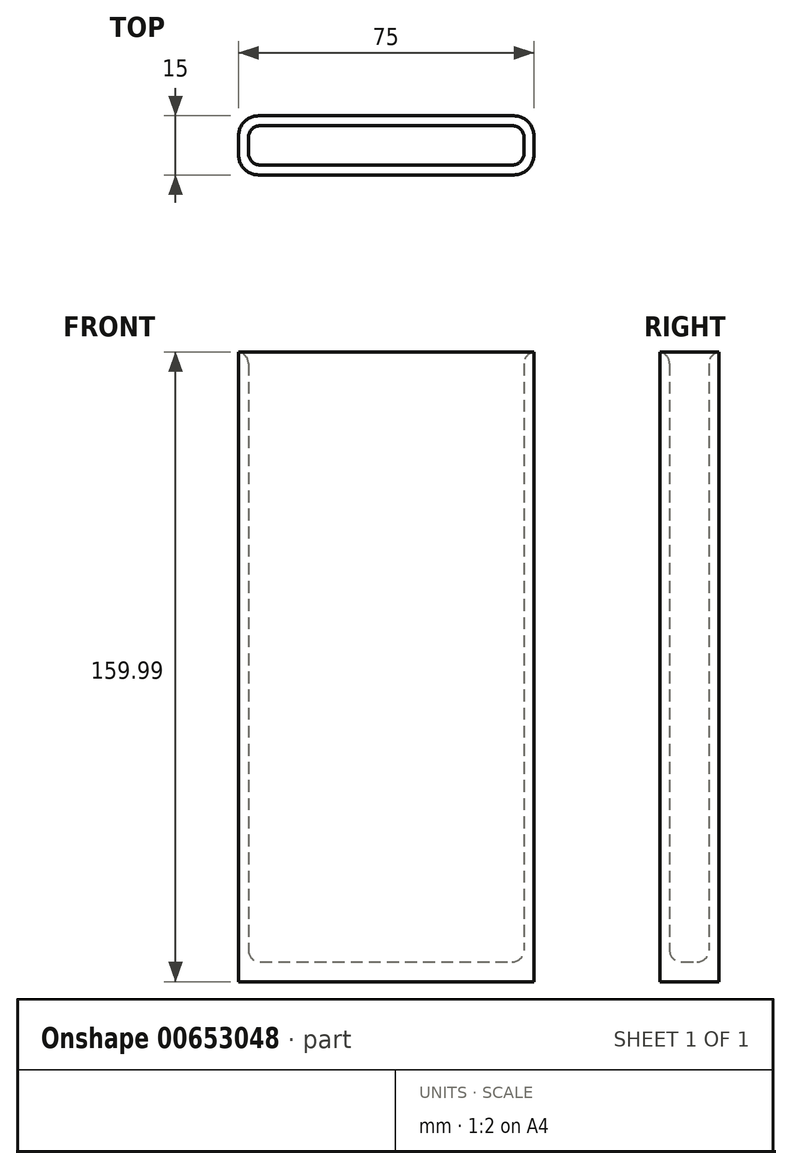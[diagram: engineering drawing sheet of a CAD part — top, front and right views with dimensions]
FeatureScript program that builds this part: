
annotation { "Feature Type Name" : "Feature", "Feature Type Description" : "" }
export const myFeature = defineFeature(function(context is Context, id is Id, definition is map)
    precondition{}
    {
        {
            var Q0;
            Q0=qCreatedBy(makeId("Top.planeOp"),FACE);
            var sketch = newSketch(context, id + "F0", { "sketchPlane" : qUnion([Q0])});
            skLineSegment(sketch, "E0.0", {"start": v(-72.5, -2.5) * mm, "end": v(2.5, -2.5) * mm});
            skLineSegment(sketch, "E0.1", {"start": v(-72.5, -2.5) * mm, "end": v(-72.5, 12.5) * mm});
            skLineSegment(sketch, "E0.2", {"start": v(2.5, 12.5) * mm, "end": v(-72.5, 12.5) * mm});
            skLineSegment(sketch, "E0.3", {"start": v(2.5, -2.5) * mm, "end": v(2.5, 12.5) * mm});
            skSolve(sketch);
        }
        {
            var Q0;
            Q0=makeQuery(id+"F0.imprint","IMPRINT",FACE,{"disambiguationData":[TD([[makeQuery(id+"F0.imprint","IMPRINT",EDGE,{"derivedFrom":sQuery(id+"F0.wireOp",EDGE,"E0.0")}),1.0]])]});
            extrude(context, id + "F1", {"entities" : qUnion([Q0]), "depth" : 5 * mm, "offsetDistance" : 25 * mm});
        }
        {
            var Q0;
            Q0=makeQuery(id+"F1.opExtrude","CAP_FACE",FACE,{"disambiguationData":[OSD([sQuery(id+"F0.wireOp",EDGE,"E0.0"),sQuery(id+"F0.wireOp",EDGE,"E0.1"),sQuery(id+"F0.wireOp",EDGE,"E0.2"),sQuery(id+"F0.wireOp",EDGE,"E0.3")])],"isStart":true});
            var sketch = newSketch(context, id + "F2", { "sketchPlane" : qUnion([Q0])});
            skLineSegment(sketch, "E1.0", {"start": v(0, 0) * mm, "end": v(-70, 0) * mm});
            skLineSegment(sketch, "E1.1", {"start": v(0, -10) * mm, "end": v(0, 0) * mm});
            skLineSegment(sketch, "E1.2", {"start": v(-70, -10) * mm, "end": v(0, -10) * mm});
            skLineSegment(sketch, "E1.3", {"start": v(-70, 0) * mm, "end": v(-70, -10) * mm});
            skSolve(sketch);
        }
        {
            var Q0;
            Q0=makeQuery(id+"F2.imprint","IMPRINT",FACE,{"disambiguationData":[TD([[makeQuery(id+"F2.imprint","IMPRINT",EDGE,{"derivedFrom":sQuery(id+"F2.wireOp",EDGE,"E1.0")}),-1.0]])]});
            extrude(context, id + "F3", {"entities" : qUnion([Q0]), "operationType" : NewBodyOperationType.ADD, "oppositeDirection" : true, "depth" : 160 * mm, "offsetDistance" : 25 * mm});
        }
        {
            var Q0;
            {var subQ0=sQuery(id+"F0.wireOp",EDGE,"E0.2");var subQ1=sQuery(id+"F0.wireOp",EDGE,"E0.1");Q0=makeQuery(id+"F3.boolean.opBoolean","MERGE",EDGE,{"derivedFrom":[makeQuery(id+"F1.opExtrude","SWEPT_EDGE",EDGE,{"disambiguationData":[OSD([subQ1,subQ0])]}),makeQuery(id+"F3.opExtrude","SWEPT_EDGE",EDGE,{"disambiguationData":[OSD([subQ1,subQ0])]})]});}
            fillet(context, id + "F4", {"entities" : qUnion([Q0]), "radius" : 5 * mm, "tangentPropagation" : true, "allowEdgeOverflow" : false});
        }
        {
            var Q0;
            {var subQ0=sQuery(id+"F0.wireOp",EDGE,"E0.1");var subQ1=sQuery(id+"F0.wireOp",EDGE,"E0.0");Q0=makeQuery(id+"F3.boolean.opBoolean","MERGE",EDGE,{"derivedFrom":[makeQuery(id+"F1.opExtrude","SWEPT_EDGE",EDGE,{"disambiguationData":[OSD([subQ1,subQ0])]}),makeQuery(id+"F3.opExtrude","SWEPT_EDGE",EDGE,{"disambiguationData":[OSD([subQ1,subQ0])]})]});}
            fillet(context, id + "F5", {"entities" : qUnion([Q0]), "radius" : 5 * mm, "tangentPropagation" : true, "allowEdgeOverflow" : false});
        }
        {
            var Q0;
            {var subQ0=sQuery(id+"F0.wireOp",EDGE,"E0.3");var subQ1=sQuery(id+"F0.wireOp",EDGE,"E0.0");Q0=makeQuery(id+"F3.boolean.opBoolean","MERGE",EDGE,{"derivedFrom":[makeQuery(id+"F1.opExtrude","SWEPT_EDGE",EDGE,{"disambiguationData":[OSD([subQ1,subQ0])]}),makeQuery(id+"F3.opExtrude","SWEPT_EDGE",EDGE,{"disambiguationData":[OSD([subQ1,subQ0])]})]});}
            fillet(context, id + "F6", {"entities" : qUnion([Q0]), "radius" : 5 * mm, "tangentPropagation" : true, "allowEdgeOverflow" : false});
        }
        {
            var Q0;
            {var subQ0=sQuery(id+"F0.wireOp",EDGE,"E0.3");var subQ1=sQuery(id+"F0.wireOp",EDGE,"E0.2");Q0=makeQuery(id+"F3.boolean.opBoolean","MERGE",EDGE,{"derivedFrom":[makeQuery(id+"F1.opExtrude","SWEPT_EDGE",EDGE,{"disambiguationData":[OSD([subQ1,subQ0])]}),makeQuery(id+"F3.opExtrude","SWEPT_EDGE",EDGE,{"disambiguationData":[OSD([subQ1,subQ0])]})]});}
            fillet(context, id + "F7", {"entities" : qUnion([Q0]), "radius" : 5 * mm, "tangentPropagation" : true, "allowEdgeOverflow" : false});
        }
        {
            var Q0;
            Q0=makeQuery(id+"F3.opExtrude","SWEPT_EDGE",EDGE,{"disambiguationData":[OSD([sQuery(id+"F2.wireOp",EDGE,"E1.2"),sQuery(id+"F2.wireOp",EDGE,"E1.3")])]});
            fillet(context, id + "F8", {"entities" : qUnion([Q0]), "radius" : 3 * mm, "tangentPropagation" : true, "allowEdgeOverflow" : false});
        }
        {
            var Q0;
            Q0=makeQuery(id+"F3.opExtrude","SWEPT_EDGE",EDGE,{"disambiguationData":[OSD([sQuery(id+"F2.wireOp",EDGE,"E1.1"),sQuery(id+"F2.wireOp",EDGE,"E1.2")])]});
            fillet(context, id + "F9", {"entities" : qUnion([Q0]), "radius" : 3 * mm, "tangentPropagation" : true, "allowEdgeOverflow" : false});
        }
        {
            var Q0;
            Q0=makeQuery(id+"F3.opExtrude","SWEPT_EDGE",EDGE,{"disambiguationData":[OSD([sQuery(id+"F2.wireOp",EDGE,"E1.0"),sQuery(id+"F2.wireOp",EDGE,"E1.3")])]});
            fillet(context, id + "F10", {"entities" : qUnion([Q0]), "radius" : 3 * mm, "tangentPropagation" : true, "allowEdgeOverflow" : false});
        }
        {
            var Q0;
            Q0=makeQuery(id+"F3.opExtrude","SWEPT_EDGE",EDGE,{"disambiguationData":[OSD([sQuery(id+"F2.wireOp",EDGE,"E1.0"),sQuery(id+"F2.wireOp",EDGE,"E1.1")])]});
            fillet(context, id + "F11", {"entities" : qUnion([Q0]), "radius" : 3 * mm, "tangentPropagation" : true, "allowEdgeOverflow" : false});
        }
        {
            var Q0;
            Q0=makeQuery(id+"F3.opExtrude","CAP_EDGE",EDGE,{"disambiguationData":[OSD([sQuery(id+"F2.wireOp",EDGE,"E1.3")])],"isStart":false});
            var Q1;
            {var subQ0=sQuery(id+"F2.wireOp",EDGE,"E1.3");var subQ1=sQuery(id+"F2.wireOp",EDGE,"E1.2");Q1=makeQuery(id+"F8.opFillet","BLEND_EDGE",EDGE,{"blendedFrom":[makeQuery(id+"F3.opExtrude","SWEPT_EDGE",EDGE,{"disambiguationData":[OSD([subQ1,subQ0])]}),makeQuery(id+"F3.opExtrude","CAP_FACE",FACE,{"disambiguationData":[OSD([sQuery(id+"F0.wireOp",EDGE,"E0.0"),sQuery(id+"F0.wireOp",EDGE,"E0.1"),sQuery(id+"F0.wireOp",EDGE,"E0.2"),sQuery(id+"F0.wireOp",EDGE,"E0.3"),sQuery(id+"F2.wireOp",EDGE,"E1.0"),sQuery(id+"F2.wireOp",EDGE,"E1.1"),subQ1,subQ0])],"isStart":false})],"blendedInto":[makeQuery(id+"F3.opExtrude","CAP_FACE",FACE,{"disambiguationData":[OSD([sQuery(id+"F0.wireOp",EDGE,"E0.0"),sQuery(id+"F0.wireOp",EDGE,"E0.1"),sQuery(id+"F0.wireOp",EDGE,"E0.2"),sQuery(id+"F0.wireOp",EDGE,"E0.3"),sQuery(id+"F2.wireOp",EDGE,"E1.0"),sQuery(id+"F2.wireOp",EDGE,"E1.1"),subQ1,subQ0])],"isStart":false})]});}
            var Q2;
            Q2=makeQuery(id+"F3.opExtrude","CAP_EDGE",EDGE,{"disambiguationData":[OSD([sQuery(id+"F2.wireOp",EDGE,"E1.2")])],"isStart":false});
            var Q3;
            {var subQ0=sQuery(id+"F2.wireOp",EDGE,"E1.2");var subQ1=sQuery(id+"F2.wireOp",EDGE,"E1.1");Q3=makeQuery(id+"F9.opFillet","BLEND_EDGE",EDGE,{"blendedFrom":[makeQuery(id+"F3.opExtrude","SWEPT_EDGE",EDGE,{"disambiguationData":[OSD([subQ1,subQ0])]}),makeQuery(id+"F3.opExtrude","CAP_FACE",FACE,{"disambiguationData":[OSD([sQuery(id+"F0.wireOp",EDGE,"E0.0"),sQuery(id+"F0.wireOp",EDGE,"E0.1"),sQuery(id+"F0.wireOp",EDGE,"E0.2"),sQuery(id+"F0.wireOp",EDGE,"E0.3"),sQuery(id+"F2.wireOp",EDGE,"E1.0"),subQ1,subQ0,sQuery(id+"F2.wireOp",EDGE,"E1.3")])],"isStart":false})],"blendedInto":[makeQuery(id+"F3.opExtrude","CAP_FACE",FACE,{"disambiguationData":[OSD([sQuery(id+"F0.wireOp",EDGE,"E0.0"),sQuery(id+"F0.wireOp",EDGE,"E0.1"),sQuery(id+"F0.wireOp",EDGE,"E0.2"),sQuery(id+"F0.wireOp",EDGE,"E0.3"),sQuery(id+"F2.wireOp",EDGE,"E1.0"),subQ1,subQ0,sQuery(id+"F2.wireOp",EDGE,"E1.3")])],"isStart":false})]});}
            var Q4;
            Q4=makeQuery(id+"F3.opExtrude","CAP_EDGE",EDGE,{"disambiguationData":[OSD([sQuery(id+"F2.wireOp",EDGE,"E1.0")])],"isStart":false});
            var Q5;
            {var subQ0=sQuery(id+"F2.wireOp",EDGE,"E1.3");var subQ1=sQuery(id+"F2.wireOp",EDGE,"E1.0");Q5=makeQuery(id+"F10.opFillet","BLEND_EDGE",EDGE,{"blendedFrom":[makeQuery(id+"F3.opExtrude","SWEPT_EDGE",EDGE,{"disambiguationData":[OSD([subQ1,subQ0])]}),makeQuery(id+"F3.opExtrude","CAP_FACE",FACE,{"disambiguationData":[OSD([sQuery(id+"F0.wireOp",EDGE,"E0.0"),sQuery(id+"F0.wireOp",EDGE,"E0.1"),sQuery(id+"F0.wireOp",EDGE,"E0.2"),sQuery(id+"F0.wireOp",EDGE,"E0.3"),subQ1,sQuery(id+"F2.wireOp",EDGE,"E1.1"),sQuery(id+"F2.wireOp",EDGE,"E1.2"),subQ0])],"isStart":false})],"blendedInto":[makeQuery(id+"F3.opExtrude","CAP_FACE",FACE,{"disambiguationData":[OSD([sQuery(id+"F0.wireOp",EDGE,"E0.0"),sQuery(id+"F0.wireOp",EDGE,"E0.1"),sQuery(id+"F0.wireOp",EDGE,"E0.2"),sQuery(id+"F0.wireOp",EDGE,"E0.3"),subQ1,sQuery(id+"F2.wireOp",EDGE,"E1.1"),sQuery(id+"F2.wireOp",EDGE,"E1.2"),subQ0])],"isStart":false})]});}
            var Q6;
            Q6=makeQuery(id+"F3.opExtrude","CAP_EDGE",EDGE,{"disambiguationData":[OSD([sQuery(id+"F2.wireOp",EDGE,"E1.1")])],"isStart":false});
            var Q7;
            {var subQ0=sQuery(id+"F2.wireOp",EDGE,"E1.1");var subQ1=sQuery(id+"F2.wireOp",EDGE,"E1.0");Q7=makeQuery(id+"F11.opFillet","BLEND_EDGE",EDGE,{"blendedFrom":[makeQuery(id+"F3.opExtrude","SWEPT_EDGE",EDGE,{"disambiguationData":[OSD([subQ1,subQ0])]}),makeQuery(id+"F3.opExtrude","CAP_FACE",FACE,{"disambiguationData":[OSD([sQuery(id+"F0.wireOp",EDGE,"E0.0"),sQuery(id+"F0.wireOp",EDGE,"E0.1"),sQuery(id+"F0.wireOp",EDGE,"E0.2"),sQuery(id+"F0.wireOp",EDGE,"E0.3"),subQ1,subQ0,sQuery(id+"F2.wireOp",EDGE,"E1.2"),sQuery(id+"F2.wireOp",EDGE,"E1.3")])],"isStart":false})],"blendedInto":[makeQuery(id+"F3.opExtrude","CAP_FACE",FACE,{"disambiguationData":[OSD([sQuery(id+"F0.wireOp",EDGE,"E0.0"),sQuery(id+"F0.wireOp",EDGE,"E0.1"),sQuery(id+"F0.wireOp",EDGE,"E0.2"),sQuery(id+"F0.wireOp",EDGE,"E0.3"),subQ1,subQ0,sQuery(id+"F2.wireOp",EDGE,"E1.2"),sQuery(id+"F2.wireOp",EDGE,"E1.3")])],"isStart":false})]});}
            fillet(context, id + "F12", {"entities" : qUnion([Q0, Q1, Q2, Q3, Q4, Q5, Q6, Q7]), "radius" : 3 * mm, "tangentPropagation" : true, "allowEdgeOverflow" : false});
        }
        {
            var Q0;
            Q0=makeQuery(id+"F3.boolean.opBoolean","INTERSECT",EDGE,{"derivedFrom":[makeQuery(id+"F1.opExtrude","CAP_FACE",FACE,{"disambiguationData":[OSD([sQuery(id+"F0.wireOp",EDGE,"E0.0"),sQuery(id+"F0.wireOp",EDGE,"E0.1"),sQuery(id+"F0.wireOp",EDGE,"E0.2"),sQuery(id+"F0.wireOp",EDGE,"E0.3")])],"isStart":false}),makeQuery(id+"F3.opExtrude","SWEPT_FACE",FACE,{"disambiguationData":[OSD([sQuery(id+"F2.wireOp",EDGE,"E1.2")])]})]});
            fillet(context, id + "F13", {"entities" : qUnion([Q0]), "radius" : 3 * mm, "tangentPropagation" : true, "allowEdgeOverflow" : false});
        }
    });
